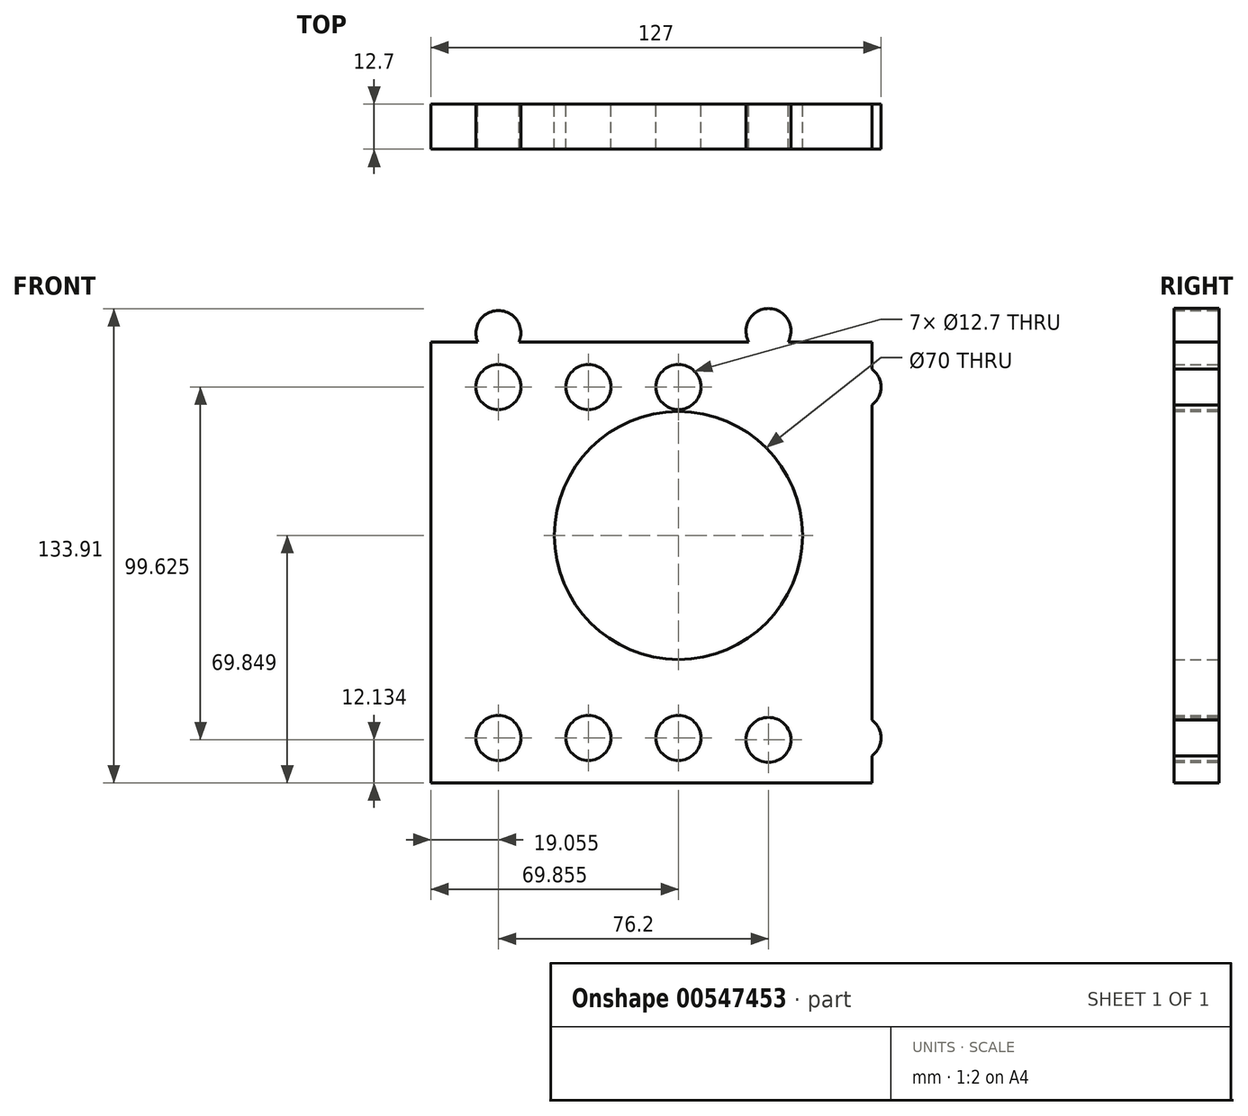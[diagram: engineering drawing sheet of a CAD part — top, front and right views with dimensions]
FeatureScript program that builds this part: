
annotation { "Feature Type Name" : "Feature", "Feature Type Description" : "" }
export const myFeature = defineFeature(function(context is Context, id is Id, definition is map)
    precondition{}
    {
        {
            var Q0;
            Q0=qCreatedBy(makeId("Front.planeOp"),FACE);
            var sketch = newSketch(context, id + "F0", { "sketchPlane" : qUnion([Q0])});
            skLineSegment(sketch, "E0.bottom", {"start": v(-67.45, 69.4) * mm, "end": v(57.01, 69.4) * mm});
            skLineSegment(sketch, "E0.top", {"start": v(-67.45, -55.05) * mm, "end": v(57.01, -55.05) * mm});
            skLineSegment(sketch, "E0.left", {"start": v(-67.45, 69.4) * mm, "end": v(-67.45, -55.05) * mm});
            skLineSegment(sketch, "E0.right", {"start": v(57.01, 69.4) * mm, "end": v(57.01, -55.05) * mm});
            skCircle(sketch, "E1", {"center": v(-48.4, 56.7) * mm, "radius": 6.35 * mm});
            skPoint(sketch, "E2.startSnap0", {"position": v(-67.45, 7.18) * mm});
            skCircle(sketch, "E3.MirrorC", {"center": v(-48.4, 71.95) * mm, "radius": 6.35 * mm});
            skCircle(sketch, "E4.MirrorC", {"center": v(-48.4, -42.35) * mm, "radius": 6.35 * mm});
            skCircle(sketch, "E5", {"center": v(-23, 56.7) * mm, "radius": 6.35 * mm});
            skCircle(sketch, "E6", {"center": v(2.4, 56.7) * mm, "radius": 6.35 * mm});
            skCircle(sketch, "E7", {"center": v(27.8, 72.51) * mm, "radius": 6.35 * mm});
            skCircle(sketch, "E8", {"center": v(53.2, 56.7) * mm, "radius": 6.35 * mm});
            skCircle(sketch, "E9.MirrorC", {"center": v(-23, -42.35) * mm, "radius": 6.35 * mm});
            skCircle(sketch, "E10.MirrorC", {"center": v(2.4, -42.35) * mm, "radius": 6.35 * mm});
            skCircle(sketch, "E11.MirrorC", {"center": v(27.8, -42.92) * mm, "radius": 6.35 * mm});
            skCircle(sketch, "E12.MirrorC", {"center": v(53.2, -42.35) * mm, "radius": 6.35 * mm});
            skCircle(sketch, "E13", {"center": v(2.4, 14.8) * mm, "radius": 35 * mm});
            skSolve(sketch);
        }
        {
            var Q0;
            Q0 = qSketchRegion(id + "F0", true);
            extrude(context, id + "F1", {"entities" : qUnion([Q0]), "depth" : 12.7 * mm, "offsetDistance" : 25.4 * mm});
        }
    });
